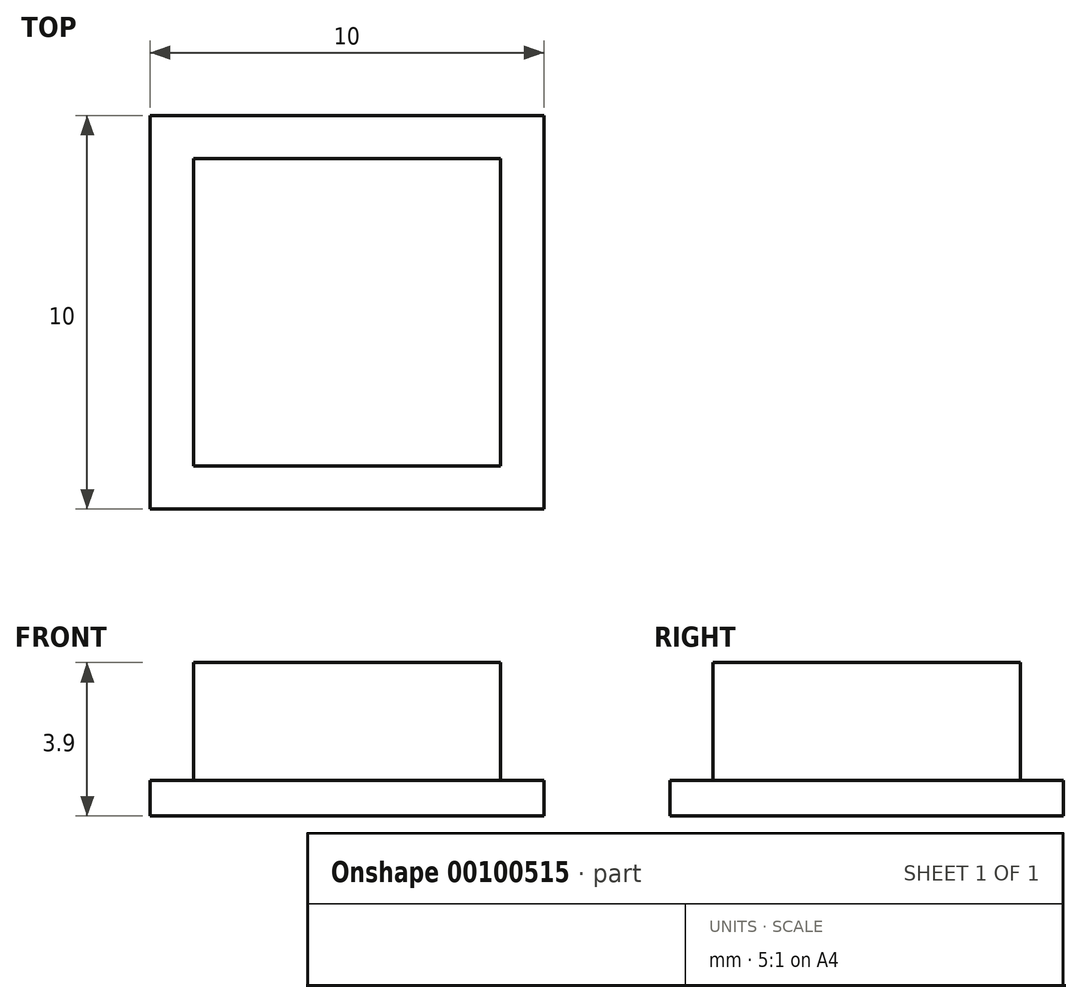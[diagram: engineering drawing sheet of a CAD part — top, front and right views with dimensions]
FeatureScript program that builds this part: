
annotation { "Feature Type Name" : "Feature", "Feature Type Description" : "" }
export const myFeature = defineFeature(function(context is Context, id is Id, definition is map)
    precondition{}
    {
        {
            var Q0;
            Q0=qCreatedBy(makeId("Top.planeOp"),FACE);
            var sketch = newSketch(context, id + "F0", { "sketchPlane" : qUnion([Q0])});
            skLineSegment(sketch, "E0.bottom", {"start": v(5, 5) * mm, "end": v(-5, 5) * mm});
            skLineSegment(sketch, "E0.top", {"start": v(5, -5) * mm, "end": v(-5, -5) * mm});
            skLineSegment(sketch, "E0.left", {"start": v(5, 5) * mm, "end": v(5, -5) * mm});
            skLineSegment(sketch, "E0.right", {"start": v(-5, 5) * mm, "end": v(-5, -5) * mm});
            skPoint(sketch, "E0.middle", {"position": v(0, 0) * mm});
            skSolve(sketch);
        }
        {
            var Q0;
            Q0 = qSketchRegion(id + "F0", true);
            extrude(context, id + "F1", {"entities" : qUnion([Q0]), "depth" : .9 * mm});
        }
        {
            var Q0;
            Q0=makeQuery(id+"F1.opExtrude","CAP_FACE",FACE,{"disambiguationData":[OSD([sQuery(id+"F0.wireOp",EDGE,"E0.bottom"),sQuery(id+"F0.wireOp",EDGE,"E0.top"),sQuery(id+"F0.wireOp",EDGE,"E0.left"),sQuery(id+"F0.wireOp",EDGE,"E0.right")])],"isStart":false});
            var sketch = newSketch(context, id + "F2", { "sketchPlane" : qUnion([Q0])});
            skLineSegment(sketch, "E1.bottom", {"start": v(3.9, 3.9) * mm, "end": v(-3.9, 3.9) * mm});
            skLineSegment(sketch, "E1.top", {"start": v(3.9, -3.9) * mm, "end": v(-3.9, -3.9) * mm});
            skLineSegment(sketch, "E1.left", {"start": v(3.9, 3.9) * mm, "end": v(3.9, -3.9) * mm});
            skLineSegment(sketch, "E1.right", {"start": v(-3.9, 3.9) * mm, "end": v(-3.9, -3.9) * mm});
            skPoint(sketch, "E1.middle", {"position": v(0, 0) * mm});
            skSolve(sketch);
        }
        {
            var Q0;
            Q0 = qSketchRegion(id + "F2", true);
            extrude(context, id + "F3", {"entities" : qUnion([Q0]), "operationType" : NewBodyOperationType.ADD, "depth" : 3 * mm});
        }
    });
